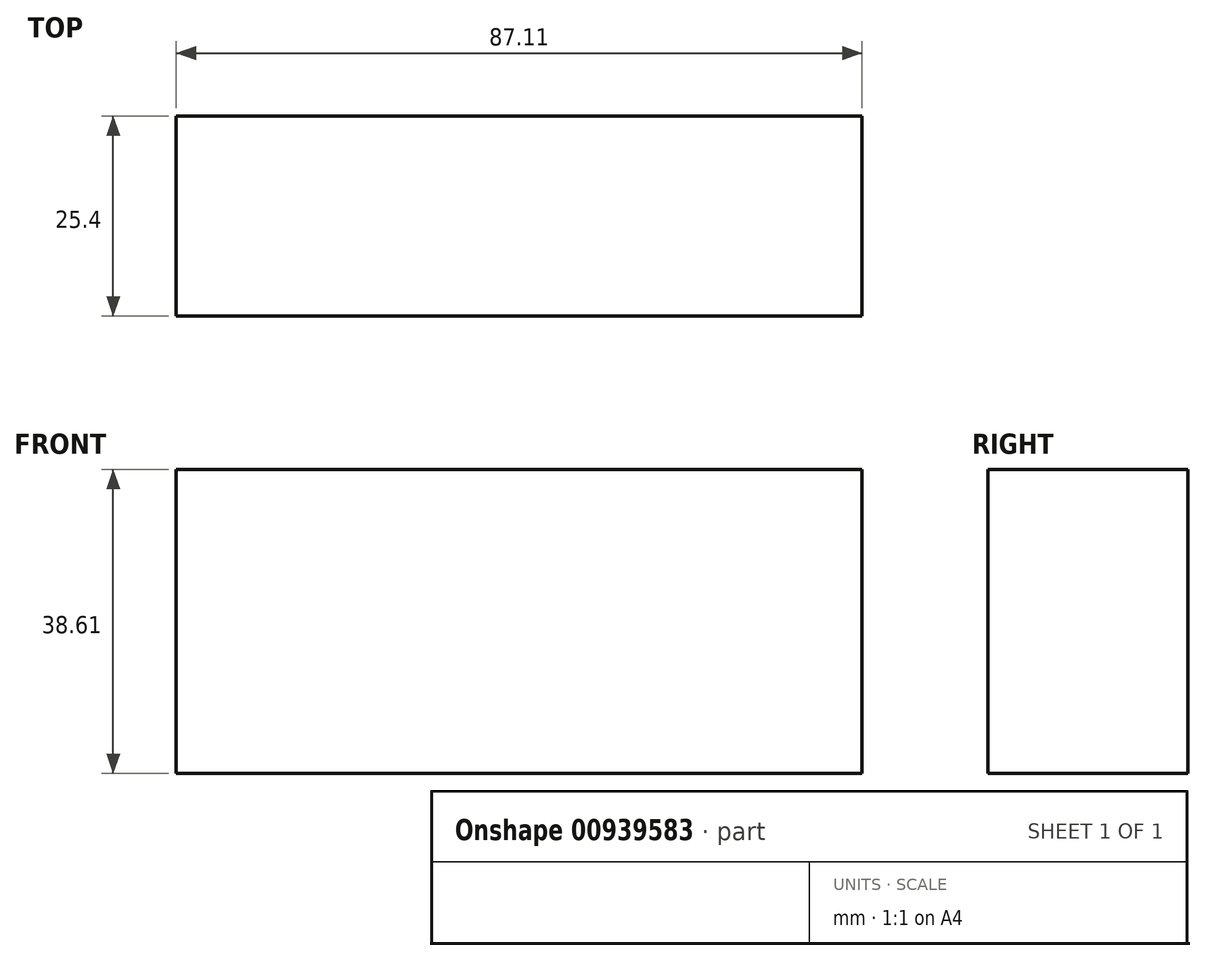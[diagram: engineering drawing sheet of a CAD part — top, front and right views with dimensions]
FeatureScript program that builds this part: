
annotation { "Feature Type Name" : "Feature", "Feature Type Description" : "" }
export const myFeature = defineFeature(function(context is Context, id is Id, definition is map)
    precondition{}
    {
        {
            var Q0;
            Q0=qCreatedBy(makeId("Front.planeOp"),FACE);
            var sketch = newSketch(context, id + "F0", { "sketchPlane" : qUnion([Q0])});
            skLineSegment(sketch, "E0.bottom", {"start": v(-161.65, 70.68) * mm, "end": v(-74.54, 70.68) * mm});
            skLineSegment(sketch, "E0.top", {"start": v(-161.65, 32.07) * mm, "end": v(-74.54, 32.07) * mm});
            skLineSegment(sketch, "E0.left", {"start": v(-161.65, 70.68) * mm, "end": v(-161.65, 32.07) * mm});
            skLineSegment(sketch, "E0.right", {"start": v(-74.54, 70.68) * mm, "end": v(-74.54, 32.07) * mm});
            skSolve(sketch);
        }
        {
            var Q0;
            Q0 = qSketchRegion(id + "F0", true);
            extrude(context, id + "F1", {"entities" : qUnion([Q0]), "depth" : 25.4 * mm, "offsetDistance" : 25.4 * mm});
        }
    });
